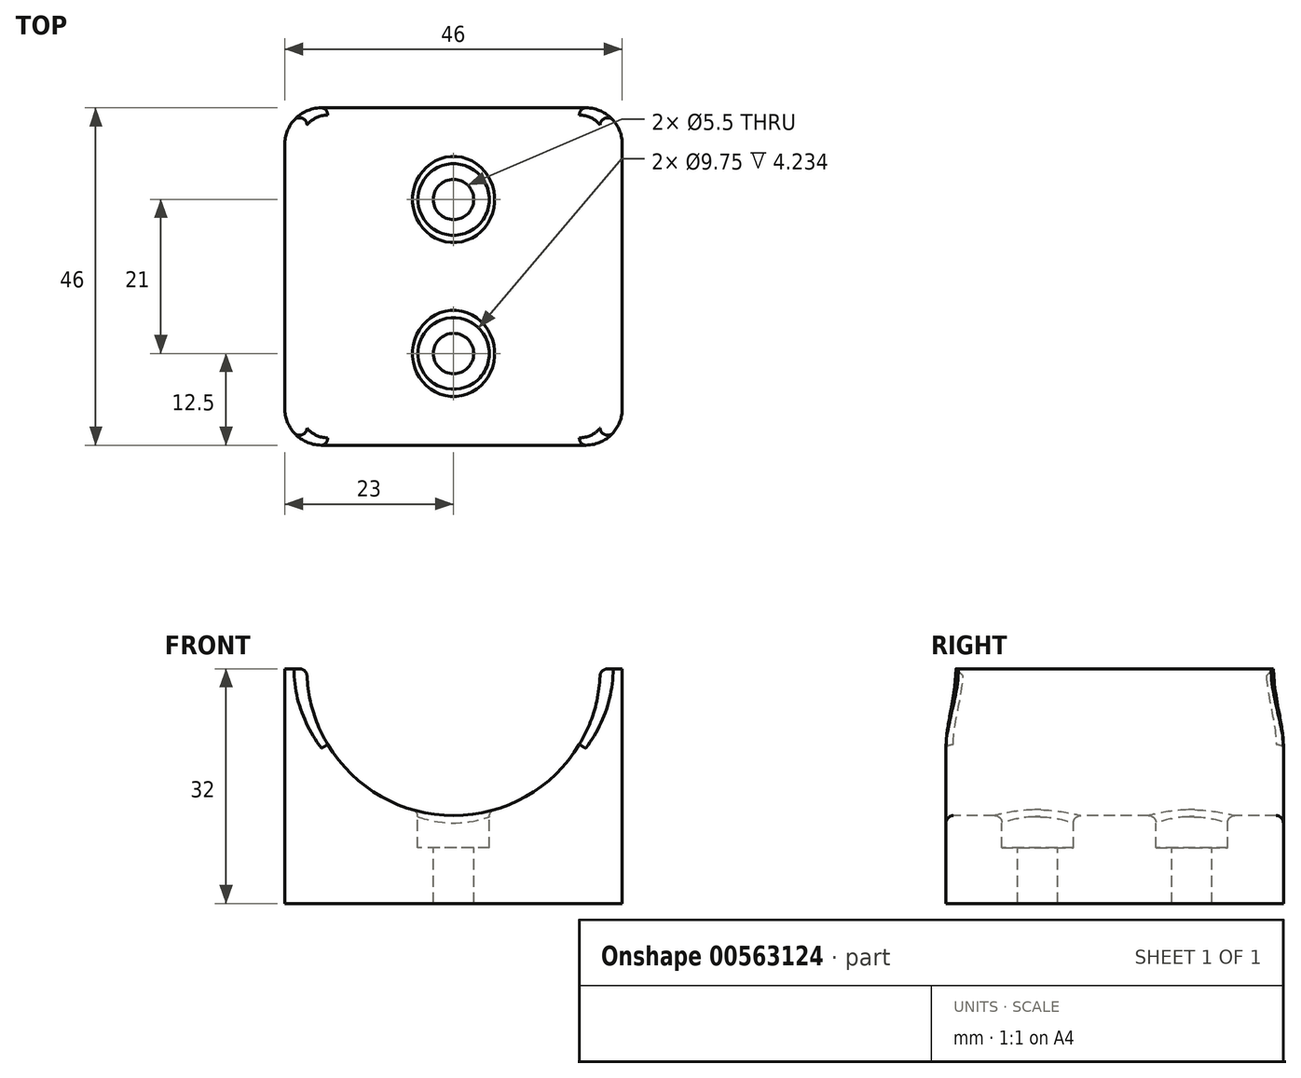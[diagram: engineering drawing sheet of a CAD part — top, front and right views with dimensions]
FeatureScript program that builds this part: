
annotation { "Feature Type Name" : "Feature", "Feature Type Description" : "" }
export const myFeature = defineFeature(function(context is Context, id is Id, definition is map)
    precondition{}
    {
        {
            var Q0;
            Q0=qCreatedBy(makeId("Top.planeOp"),FACE);
            var sketch = newSketch(context, id + "F0", { "sketchPlane" : qUnion([Q0])});
            skLineSegment(sketch, "E0.bottom", {"start": v(23, -23) * mm, "end": v(-23, -23) * mm});
            skLineSegment(sketch, "E0.top", {"start": v(23, 23) * mm, "end": v(-23, 23) * mm});
            skLineSegment(sketch, "E0.left", {"start": v(23, -23) * mm, "end": v(23, 23) * mm});
            skLineSegment(sketch, "E0.right", {"start": v(-23, -23) * mm, "end": v(-23, 23) * mm});
            skPoint(sketch, "E0.middle", {"position": v(0, 0) * mm});
            skSolve(sketch);
        }
        {
            var Q0;
            Q0 = qSketchRegion(id + "F0", true);
            extrude(context, id + "F1", {"entities" : qUnion([Q0]), "depth" : 32 * mm, "offsetDistance" : 25 * mm});
        }
        {
            var Q0;
            Q0=makeQuery(id+"F1.opExtrude","SWEPT_FACE",FACE,{"disambiguationData":[OSD([sQuery(id+"F0.wireOp",EDGE,"E0.bottom")])]});
            var sketch = newSketch(context, id + "F2", { "sketchPlane" : qUnion([Q0])});
            skCircle(sketch, "E1", {"center": v(0, 32) * mm, "radius": 20 * mm});
            skSolve(sketch);
        }
        {
            var Q0;
            Q0 = qSketchRegion(id + "F2", true);
            extrude(context, id + "F3", {"entities" : qUnion([Q0]), "operationType" : NewBodyOperationType.REMOVE, "endBound" : BoundingType.THROUGH_ALL, "oppositeDirection" : true, "depth" : 25 * mm, "offsetDistance" : 25 * mm});
        }
        {
            var Q0;
            Q0=qCreatedBy(makeId("Top.planeOp"),FACE);
            cPlane(context, id + "F4", {"entities" : qUnion([Q0]), "cplaneType" : CPlaneType.OFFSET, "offset" : 12.6 * mm, "width" : 150 * mm, "height" : 150 * mm});
        }
        {
            var Q0;
            Q0=qCreatedBy(id+"F4.planeOp",FACE);
            var sketch = newSketch(context, id + "F5", { "sketchPlane" : qUnion([Q0])});
            skLineSegment(sketch, "E2", {"start": v(0, 23) * mm, "end": v(0, -23) * mm, "construction": true});
            skLineSegment(sketch, "E3", {"start": v(-20, 0) * mm, "end": v(20, 0) * mm, "construction": true});
            skPoint(sketch, "E4", {"position": v(0, 10.5) * mm});
            skPoint(sketch, "E5.MirrorP", {"position": v(0, -10.5) * mm});
            skSolve(sketch);
        }
        {
            var Q0;
            Q0=sQuery(id+"F5.wireOp",VERTEX,"E4");
            var Q1;
            Q1=sQuery(id+"F5.wireOp",VERTEX,"E5.MirrorP");
            var Q2;
            Q2=makeQuery(id+"F1.opExtrude","SWEPT_BODY",BODY,{"disambiguationData":[OSD([sQuery(id+"F0.wireOp",EDGE,"E0.bottom"),sQuery(id+"F0.wireOp",EDGE,"E0.top"),sQuery(id+"F0.wireOp",EDGE,"E0.left"),sQuery(id+"F0.wireOp",EDGE,"E0.right")])]});
            hole(context, id + "F6", {"style" : HoleStyle.C_BORE, "endStyle" : HoleEndStyle.THROUGH, "standardTappedOrClearance" : lookupTablePath({ "standard" : "ISO", "fit" : "Normal", "size" : "M5", "type" : "Clearance" }), "standardBlindInLast" : lookupTablePath({ "fit" : "Standard", "standard" : "ISO", "size" : "M5", "type" : "Clearance" }), "holeDiameter" : 5.5 * mm, "cBoreDiameter" : 9.75 * mm, "cBoreDepth" : 5 * mm, "majorDiameter" : 5 * mm, "isTappedThrough" : true, "tappedDepth" : 12 * mm, "tapClearance" : 3, "startFromSketch" : true, "locations" : qUnion([Q0, Q1]), "scope" : qUnion([Q2])});
        }
        {
            var Q0;
            Q0=makeQuery(id+"F1.opExtrude","SWEPT_EDGE",EDGE,{"disambiguationData":[OSD([sQuery(id+"F0.wireOp",EDGE,"E0.bottom"),sQuery(id+"F0.wireOp",EDGE,"E0.left")])]});
            var Q1;
            Q1=makeQuery(id+"F1.opExtrude","SWEPT_EDGE",EDGE,{"disambiguationData":[OSD([sQuery(id+"F0.wireOp",EDGE,"E0.bottom"),sQuery(id+"F0.wireOp",EDGE,"E0.right")])]});
            var Q2;
            Q2=makeQuery(id+"F1.opExtrude","SWEPT_EDGE",EDGE,{"disambiguationData":[OSD([sQuery(id+"F0.wireOp",EDGE,"E0.top"),sQuery(id+"F0.wireOp",EDGE,"E0.right")])]});
            var Q3;
            Q3=makeQuery(id+"F1.opExtrude","SWEPT_EDGE",EDGE,{"disambiguationData":[OSD([sQuery(id+"F0.wireOp",EDGE,"E0.top"),sQuery(id+"F0.wireOp",EDGE,"E0.left")])]});
            fillet(context, id + "F7", {"entities" : qUnion([Q0, Q1, Q2, Q3]), "radius" : 5 * mm, "tangentPropagation" : true, "allowEdgeOverflow" : false});
        }
        {
            var Q0;
            Q0=makeQuery(id+"F3.boolean.opBoolean","COPY",FACE,{"derivedFrom":makeQuery(id+"F3.opExtrude","SWEPT_FACE",FACE,{"disambiguationData":[OSD([sQuery(id+"F2.wireOp",EDGE,"E1")])]})});
            fillet(context, id + "F8", {"entities" : qUnion([Q0]), "radius" : 1 * mm, "tangentPropagation" : true, "allowEdgeOverflow" : false});
        }
    });
